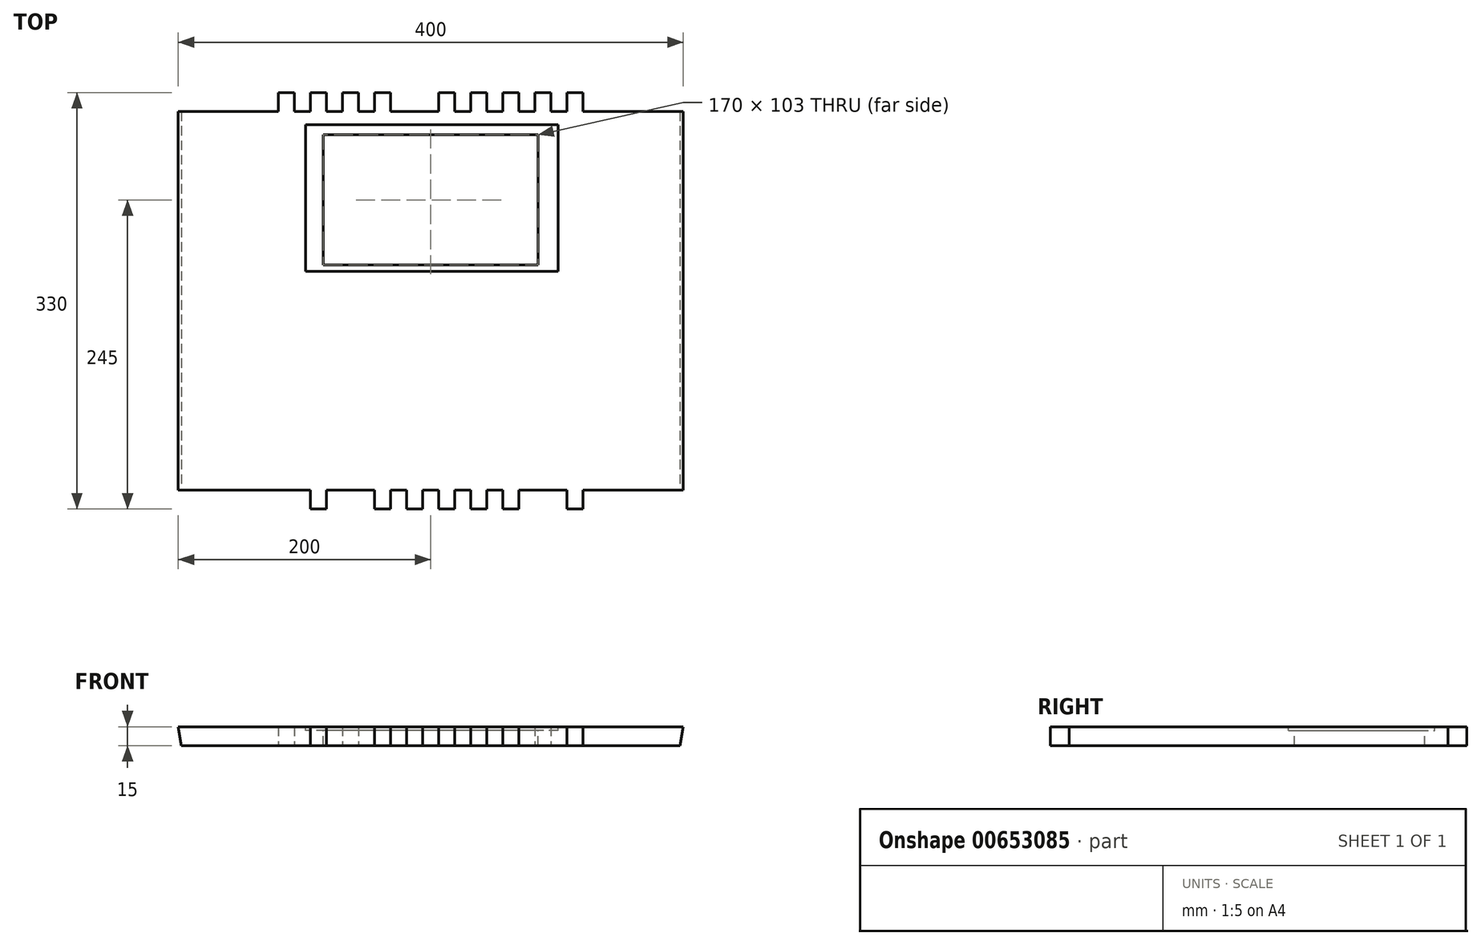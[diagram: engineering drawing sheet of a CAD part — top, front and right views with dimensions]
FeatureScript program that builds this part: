
annotation { "Feature Type Name" : "Feature", "Feature Type Description" : "" }
export const myFeature = defineFeature(function(context is Context, id is Id, definition is map)
    precondition{}
    {
        {
            var Q0;
            Q0=qCreatedBy(makeId("Top.planeOp"),FACE);
            var sketch = newSketch(context, id + "F0", { "sketchPlane" : qUnion([Q0])});
            skLineSegment(sketch, "E0.bottom", {"start": v(200, -150) * mm, "end": v(-200, -150) * mm});
            skLineSegment(sketch, "E0.top", {"start": v(200, 150) * mm, "end": v(-200, 150) * mm});
            skLineSegment(sketch, "E0.left", {"start": v(200, -150) * mm, "end": v(200, 150) * mm});
            skLineSegment(sketch, "E0.right", {"start": v(-200, -150) * mm, "end": v(-200, 150) * mm});
            skPoint(sketch, "E0.middle", {"position": v(0, 0) * mm});
            skLineSegment(sketch, "E1", {"start": v(0, 150) * mm, "end": v(-6.35, 150) * mm});
            skLineSegment(sketch, "E2.bottom", {"start": v(-6.35, 150) * mm, "end": v(-19.05, 150) * mm});
            skLineSegment(sketch, "E2.top", {"start": v(-6.35, 165) * mm, "end": v(-19.05, 165) * mm});
            skLineSegment(sketch, "E2.left", {"start": v(-6.35, 150) * mm, "end": v(-6.35, 165) * mm});
            skLineSegment(sketch, "E2.right", {"start": v(-19.05, 150) * mm, "end": v(-19.05, 165) * mm});
            skLineSegment(sketch, "E3.1.0.0", {"start": v(-31.75, 165) * mm, "end": v(-44.45, 165) * mm});
            skLineSegment(sketch, "E3.1.0.1", {"start": v(-44.45, 150) * mm, "end": v(-44.45, 165) * mm});
            skLineSegment(sketch, "E3.1.0.2", {"start": v(-31.75, 150) * mm, "end": v(-31.75, 165) * mm});
            skLineSegment(sketch, "E3.1.0.3", {"start": v(-31.75, 150) * mm, "end": v(-44.45, 150) * mm});
            skLineSegment(sketch, "E3.2.0.0", {"start": v(-57.15, 165) * mm, "end": v(-69.85, 165) * mm});
            skLineSegment(sketch, "E3.2.0.1", {"start": v(-69.85, 150) * mm, "end": v(-69.85, 165) * mm});
            skLineSegment(sketch, "E3.2.0.2", {"start": v(-57.15, 150) * mm, "end": v(-57.15, 165) * mm});
            skLineSegment(sketch, "E3.2.0.3", {"start": v(-57.15, 150) * mm, "end": v(-69.85, 150) * mm});
            skLineSegment(sketch, "E3.3.0.0", {"start": v(-82.55, 165) * mm, "end": v(-95.25, 165) * mm});
            skLineSegment(sketch, "E3.3.0.1", {"start": v(-95.25, 150) * mm, "end": v(-95.25, 165) * mm});
            skLineSegment(sketch, "E3.3.0.2", {"start": v(-82.55, 150) * mm, "end": v(-82.55, 165) * mm});
            skLineSegment(sketch, "E3.3.0.3", {"start": v(-82.55, 150) * mm, "end": v(-95.25, 150) * mm});
            skLineSegment(sketch, "E3.4.0.0", {"start": v(-107.95, 165) * mm, "end": v(-120.65, 165) * mm});
            skLineSegment(sketch, "E3.4.0.1", {"start": v(-120.65, 150) * mm, "end": v(-120.65, 165) * mm});
            skLineSegment(sketch, "E3.4.0.2", {"start": v(-107.95, 150) * mm, "end": v(-107.95, 165) * mm});
            skLineSegment(sketch, "E3.4.0.3", {"start": v(-107.95, 150) * mm, "end": v(-120.65, 150) * mm});
            skLineSegment(sketch, "E3.direction1", {"start": v(-19.05, 165) * mm, "end": v(-44.45, 165) * mm, "construction": true});
            skLineSegment(sketch, "E4.1.0.0", {"start": v(6.35, 150) * mm, "end": v(6.35, 165) * mm});
            skLineSegment(sketch, "E4.1.0.1", {"start": v(19.05, 165) * mm, "end": v(6.35, 165) * mm});
            skLineSegment(sketch, "E4.1.0.2", {"start": v(19.05, 150) * mm, "end": v(6.35, 150) * mm});
            skLineSegment(sketch, "E4.1.0.3", {"start": v(19.05, 150) * mm, "end": v(19.05, 165) * mm});
            skLineSegment(sketch, "E4.2.0.0", {"start": v(31.75, 150) * mm, "end": v(31.75, 165) * mm});
            skLineSegment(sketch, "E4.2.0.1", {"start": v(44.45, 165) * mm, "end": v(31.75, 165) * mm});
            skLineSegment(sketch, "E4.2.0.2", {"start": v(44.45, 150) * mm, "end": v(31.75, 150) * mm});
            skLineSegment(sketch, "E4.2.0.3", {"start": v(44.45, 150) * mm, "end": v(44.45, 165) * mm});
            skLineSegment(sketch, "E4.3.0.0", {"start": v(57.15, 150) * mm, "end": v(57.15, 165) * mm});
            skLineSegment(sketch, "E4.3.0.1", {"start": v(69.85, 165) * mm, "end": v(57.15, 165) * mm});
            skLineSegment(sketch, "E4.3.0.2", {"start": v(69.85, 150) * mm, "end": v(57.15, 150) * mm});
            skLineSegment(sketch, "E4.3.0.3", {"start": v(69.85, 150) * mm, "end": v(69.85, 165) * mm});
            skLineSegment(sketch, "E4.4.0.0", {"start": v(82.55, 150) * mm, "end": v(82.55, 165) * mm});
            skLineSegment(sketch, "E4.4.0.1", {"start": v(95.25, 165) * mm, "end": v(82.55, 165) * mm});
            skLineSegment(sketch, "E4.4.0.2", {"start": v(95.25, 150) * mm, "end": v(82.55, 150) * mm});
            skLineSegment(sketch, "E4.4.0.3", {"start": v(95.25, 150) * mm, "end": v(95.25, 165) * mm});
            skLineSegment(sketch, "E4.5.0.0", {"start": v(107.95, 150) * mm, "end": v(107.95, 165) * mm});
            skLineSegment(sketch, "E4.5.0.1", {"start": v(120.65, 165) * mm, "end": v(107.95, 165) * mm});
            skLineSegment(sketch, "E4.5.0.2", {"start": v(120.65, 150) * mm, "end": v(107.95, 150) * mm});
            skLineSegment(sketch, "E4.5.0.3", {"start": v(120.65, 150) * mm, "end": v(120.65, 165) * mm});
            skLineSegment(sketch, "E4.direction1", {"start": v(-19.05, 150) * mm, "end": v(6.35, 150) * mm, "construction": true});
            skLineSegment(sketch, "E5.MirrorCS", {"start": v(-19.05, -150) * mm, "end": v(-19.05, -165) * mm});
            skLineSegment(sketch, "E6.MirrorCS", {"start": v(-6.35, -150) * mm, "end": v(-19.05, -150) * mm});
            skLineSegment(sketch, "E7.MirrorCS", {"start": v(-31.75, -165) * mm, "end": v(-44.45, -165) * mm});
            skLineSegment(sketch, "E8.MirrorCS", {"start": v(0, -150) * mm, "end": v(-6.35, -150) * mm});
            skLineSegment(sketch, "E9.MirrorCS", {"start": v(-19.05, -150) * mm, "end": v(6.35, -150) * mm, "construction": true});
            skLineSegment(sketch, "E10.MirrorCS", {"start": v(-44.45, -150) * mm, "end": v(-44.45, -165) * mm});
            skLineSegment(sketch, "E11.MirrorCS", {"start": v(-82.55, -165) * mm, "end": v(-95.25, -165) * mm});
            skLineSegment(sketch, "E12.MirrorCS", {"start": v(44.45, -150) * mm, "end": v(44.45, -165) * mm});
            skLineSegment(sketch, "E13.MirrorCS", {"start": v(44.45, -150) * mm, "end": v(31.75, -150) * mm});
            skLineSegment(sketch, "E14.MirrorCS", {"start": v(-57.15, -150) * mm, "end": v(-69.85, -150) * mm});
            skLineSegment(sketch, "E15.MirrorCS", {"start": v(-82.55, -150) * mm, "end": v(-95.25, -150) * mm});
            skLineSegment(sketch, "E16.MirrorCS", {"start": v(57.15, -150) * mm, "end": v(57.15, -165) * mm});
            skLineSegment(sketch, "E17.MirrorCS", {"start": v(-107.95, -150) * mm, "end": v(-120.65, -150) * mm});
            skLineSegment(sketch, "E18.MirrorCS", {"start": v(95.25, -150) * mm, "end": v(82.55, -150) * mm});
            skLineSegment(sketch, "E19.MirrorCS", {"start": v(-69.85, -150) * mm, "end": v(-69.85, -165) * mm});
            skLineSegment(sketch, "E20.MirrorCS", {"start": v(69.85, -165) * mm, "end": v(57.15, -165) * mm});
            skLineSegment(sketch, "E21.MirrorCS", {"start": v(-82.55, -150) * mm, "end": v(-82.55, -165) * mm});
            skLineSegment(sketch, "E22.MirrorCS", {"start": v(-31.75, -150) * mm, "end": v(-31.75, -165) * mm});
            skLineSegment(sketch, "E23.MirrorCS", {"start": v(-107.95, -150) * mm, "end": v(-107.95, -165) * mm});
            skLineSegment(sketch, "E24.MirrorCS", {"start": v(69.85, -150) * mm, "end": v(57.15, -150) * mm});
            skLineSegment(sketch, "E25.MirrorCS", {"start": v(95.25, -150) * mm, "end": v(95.25, -165) * mm});
            skLineSegment(sketch, "E26.MirrorCS", {"start": v(44.45, -165) * mm, "end": v(31.75, -165) * mm});
            skLineSegment(sketch, "E27.MirrorCS", {"start": v(-120.65, -150) * mm, "end": v(-120.65, -165) * mm});
            skLineSegment(sketch, "E28.MirrorCS", {"start": v(-95.25, -150) * mm, "end": v(-95.25, -165) * mm});
            skLineSegment(sketch, "E29.MirrorCS", {"start": v(120.65, -165) * mm, "end": v(107.95, -165) * mm});
            skLineSegment(sketch, "E30.MirrorCS", {"start": v(19.05, -165) * mm, "end": v(6.35, -165) * mm});
            skLineSegment(sketch, "E31.MirrorCS", {"start": v(-31.75, -150) * mm, "end": v(-44.45, -150) * mm});
            skLineSegment(sketch, "E32.MirrorCS", {"start": v(120.65, -150) * mm, "end": v(120.65, -165) * mm});
            skLineSegment(sketch, "E33.MirrorCS", {"start": v(19.05, -150) * mm, "end": v(19.05, -165) * mm});
            skLineSegment(sketch, "E34.MirrorCS", {"start": v(120.65, -150) * mm, "end": v(107.95, -150) * mm});
            skLineSegment(sketch, "E35.MirrorCS", {"start": v(-107.95, -165) * mm, "end": v(-120.65, -165) * mm});
            skLineSegment(sketch, "E36.MirrorCS", {"start": v(6.35, -150) * mm, "end": v(6.35, -165) * mm});
            skLineSegment(sketch, "E37.MirrorCS", {"start": v(107.95, -150) * mm, "end": v(107.95, -165) * mm});
            skLineSegment(sketch, "E38.MirrorCS", {"start": v(19.05, -150) * mm, "end": v(6.35, -150) * mm});
            skLineSegment(sketch, "E39.MirrorCS", {"start": v(31.75, -150) * mm, "end": v(31.75, -165) * mm});
            skLineSegment(sketch, "E40.MirrorCS", {"start": v(-57.15, -165) * mm, "end": v(-69.85, -165) * mm});
            skLineSegment(sketch, "E41.MirrorCS", {"start": v(-57.15, -150) * mm, "end": v(-57.15, -165) * mm});
            skLineSegment(sketch, "E42.MirrorCS", {"start": v(95.25, -165) * mm, "end": v(82.55, -165) * mm});
            skLineSegment(sketch, "E43.MirrorCS", {"start": v(69.85, -150) * mm, "end": v(69.85, -165) * mm});
            skLineSegment(sketch, "E44.MirrorCS", {"start": v(82.55, -150) * mm, "end": v(82.55, -165) * mm});
            skLineSegment(sketch, "E45.MirrorCS", {"start": v(-19.05, -165) * mm, "end": v(-44.45, -165) * mm, "construction": true});
            skLineSegment(sketch, "E46.MirrorCS", {"start": v(-6.35, -165) * mm, "end": v(-19.05, -165) * mm});
            skLineSegment(sketch, "E47.MirrorCS", {"start": v(-6.35, -150) * mm, "end": v(-6.35, -165) * mm});
            skSolve(sketch);
        }
        {
            var Q0;
            {var subQ15=sQuery(id+"F0.wireOp",EDGE,"E0.left");Q0=makeQuery(id+"F0.imprint","IMPRINT",FACE,{"disambiguationData":[TD([[makeQuery(id+"F0.imprint","IMPRINT",EDGE,{"derivedFrom":subQ15}),1.0]])]});}
            var Q1;
            Q1=makeQuery(id+"F0.imprint","IMPRINT",FACE,{"disambiguationData":[TD([[makeQuery(id+"F0.imprint","IMPRINT",EDGE,{"derivedFrom":sQuery(id+"F0.wireOp",EDGE,"E7.MirrorCS")}),-1.0]])]});
            var Q2;
            Q2=makeQuery(id+"F0.imprint","IMPRINT",FACE,{"disambiguationData":[TD([[makeQuery(id+"F0.imprint","IMPRINT",EDGE,{"derivedFrom":sQuery(id+"F0.wireOp",EDGE,"E4.5.0.0")}),-1.0]])]});
            var Q3;
            Q3=makeQuery(id+"F0.imprint","IMPRINT",FACE,{"disambiguationData":[TD([[makeQuery(id+"F0.imprint","IMPRINT",EDGE,{"derivedFrom":sQuery(id+"F0.wireOp",EDGE,"E17.MirrorCS")}),1.0]])]});
            var Q4;
            Q4=makeQuery(id+"F0.imprint","IMPRINT",FACE,{"disambiguationData":[TD([[makeQuery(id+"F0.imprint","IMPRINT",EDGE,{"derivedFrom":sQuery(id+"F0.wireOp",EDGE,"E29.MirrorCS")}),-1.0]])]});
            var Q5;
            Q5=makeQuery(id+"F0.imprint","IMPRINT",FACE,{"disambiguationData":[TD([[makeQuery(id+"F0.imprint","IMPRINT",EDGE,{"derivedFrom":sQuery(id+"F0.wireOp",EDGE,"E30.MirrorCS")}),-1.0]])]});
            var Q6;
            Q6=makeQuery(id+"F0.imprint","IMPRINT",FACE,{"disambiguationData":[TD([[makeQuery(id+"F0.imprint","IMPRINT",EDGE,{"derivedFrom":sQuery(id+"F0.wireOp",EDGE,"E16.MirrorCS")}),1.0]])]});
            var Q7;
            Q7=makeQuery(id+"F0.imprint","IMPRINT",FACE,{"disambiguationData":[TD([[makeQuery(id+"F0.imprint","IMPRINT",EDGE,{"derivedFrom":sQuery(id+"F0.wireOp",EDGE,"E14.MirrorCS")}),1.0]])]});
            var Q8;
            Q8=makeQuery(id+"F0.imprint","IMPRINT",FACE,{"disambiguationData":[TD([[makeQuery(id+"F0.imprint","IMPRINT",EDGE,{"derivedFrom":sQuery(id+"F0.wireOp",EDGE,"E3.2.0.0")}),1.0]])]});
            var Q9;
            Q9=makeQuery(id+"F0.imprint","IMPRINT",FACE,{"disambiguationData":[TD([[makeQuery(id+"F0.imprint","IMPRINT",EDGE,{"derivedFrom":sQuery(id+"F0.wireOp",EDGE,"E4.1.0.0")}),-1.0]])]});
            var Q10;
            Q10=makeQuery(id+"F0.imprint","IMPRINT",FACE,{"disambiguationData":[TD([[makeQuery(id+"F0.imprint","IMPRINT",EDGE,{"derivedFrom":sQuery(id+"F0.wireOp",EDGE,"E3.3.0.0")}),1.0]])]});
            var Q11;
            Q11=makeQuery(id+"F0.imprint","IMPRINT",FACE,{"disambiguationData":[TD([[makeQuery(id+"F0.imprint","IMPRINT",EDGE,{"derivedFrom":sQuery(id+"F0.wireOp",EDGE,"E11.MirrorCS")}),-1.0]])]});
            var Q12;
            Q12=makeQuery(id+"F0.imprint","IMPRINT",FACE,{"disambiguationData":[TD([[makeQuery(id+"F0.imprint","IMPRINT",EDGE,{"derivedFrom":sQuery(id+"F0.wireOp",EDGE,"E4.2.0.0")}),-1.0]])]});
            var Q13;
            Q13=makeQuery(id+"F0.imprint","IMPRINT",FACE,{"disambiguationData":[TD([[makeQuery(id+"F0.imprint","IMPRINT",EDGE,{"derivedFrom":sQuery(id+"F0.wireOp",EDGE,"E18.MirrorCS")}),1.0]])]});
            var Q14;
            Q14=makeQuery(id+"F0.imprint","IMPRINT",FACE,{"disambiguationData":[TD([[makeQuery(id+"F0.imprint","IMPRINT",EDGE,{"derivedFrom":sQuery(id+"F0.wireOp",EDGE,"E12.MirrorCS")}),-1.0]])]});
            var Q15;
            Q15=makeQuery(id+"F0.imprint","IMPRINT",FACE,{"disambiguationData":[TD([[makeQuery(id+"F0.imprint","IMPRINT",EDGE,{"derivedFrom":sQuery(id+"F0.wireOp",EDGE,"E3.1.0.0")}),1.0]])]});
            var Q16;
            Q16=makeQuery(id+"F0.imprint","IMPRINT",FACE,{"disambiguationData":[TD([[makeQuery(id+"F0.imprint","IMPRINT",EDGE,{"derivedFrom":sQuery(id+"F0.wireOp",EDGE,"E3.4.0.0")}),1.0]])]});
            var Q17;
            Q17=makeQuery(id+"F0.imprint","IMPRINT",FACE,{"disambiguationData":[TD([[makeQuery(id+"F0.imprint","IMPRINT",EDGE,{"derivedFrom":sQuery(id+"F0.wireOp",EDGE,"E4.4.0.0")}),-1.0]])]});
            var Q18;
            Q18=makeQuery(id+"F0.imprint","IMPRINT",FACE,{"disambiguationData":[TD([[makeQuery(id+"F0.imprint","IMPRINT",EDGE,{"derivedFrom":sQuery(id+"F0.wireOp",EDGE,"E4.3.0.0")}),-1.0]])]});
            var Q19;
            Q19=makeQuery(id+"F0.imprint","IMPRINT",FACE,{"disambiguationData":[TD([[makeQuery(id+"F0.imprint","IMPRINT",EDGE,{"derivedFrom":sQuery(id+"F0.wireOp",EDGE,"E2.bottom")}),-1.0]])]});
            var Q20;
            Q20=makeQuery(id+"F0.imprint","IMPRINT",FACE,{"disambiguationData":[TD([[makeQuery(id+"F0.imprint","IMPRINT",EDGE,{"derivedFrom":sQuery(id+"F0.wireOp",EDGE,"E5.MirrorCS")}),1.0]])]});
            extrude(context, id + "F1", {"entities" : qUnion([Q0, Q1, Q2, Q3, Q4, Q5, Q6, Q7, Q8, Q9, Q10, Q11, Q12, Q13, Q14, Q15, Q16, Q17, Q18, Q19, Q20]), "depth" : 15 * mm, "offsetDistance" : 25 * mm});
        }
        {
            var Q0;
            {var subQ0=sQuery(id+"F0.wireOp",EDGE,"E0.bottom");Q0=makeQuery(id+"F1.opExtrude","SWEPT_FACE",FACE,{"disambiguationData":[OSD([subQ0]),TDD([makeQuery(id+"F0.imprint","IMPRINT",EDGE,{"disambiguationData":[TD([[makeQuery(id+"F0.imprint","INTERSECT",VERTEX,{"derivedFrom":[subQ0,sQuery(id+"F0.wireOp",EDGE,"E0.right")]}),1.0]])],"derivedFrom":subQ0})])]});}
            var sketch = newSketch(context, id + "F2", { "sketchPlane" : qUnion([Q0])});
            skLineSegment(sketch, "E48", {"start": v(-197.5, 0) * mm, "end": v(-200, 0) * mm});
            skLineSegment(sketch, "E49", {"start": v(-200, 0) * mm, "end": v(-200, 15) * mm});
            skLineSegment(sketch, "E50", {"start": v(-200, 15) * mm, "end": v(-197.5, 0) * mm});
            skSolve(sketch);
        }
        {
            var Q0;
            Q0=makeQuery(id+"F2.imprint","IMPRINT",FACE,{"disambiguationData":[TD([[makeQuery(id+"F2.imprint","IMPRINT",EDGE,{"derivedFrom":sQuery(id+"F2.wireOp",EDGE,"E48")}),-1.0]])]});
            extrude(context, id + "F3", {"entities" : qUnion([Q0]), "operationType" : NewBodyOperationType.REMOVE, "endBound" : BoundingType.THROUGH_ALL, "oppositeDirection" : true, "depth" : 25 * mm, "offsetDistance" : 25 * mm});
        }
        {
            var Q0;
            {var subQ0=sQuery(id+"F0.wireOp",EDGE,"E0.bottom");Q0=makeQuery(id+"F1.opExtrude","SWEPT_FACE",FACE,{"disambiguationData":[OSD([subQ0]),TDD([makeQuery(id+"F0.imprint","IMPRINT",EDGE,{"disambiguationData":[TD([[makeQuery(id+"F0.imprint","INTERSECT",VERTEX,{"derivedFrom":[subQ0,sQuery(id+"F0.wireOp",EDGE,"E0.left")]}),-1.0]])],"derivedFrom":subQ0})])]});}
            var sketch = newSketch(context, id + "F4", { "sketchPlane" : qUnion([Q0])});
            skLineSegment(sketch, "E51", {"start": v(197.5, 0) * mm, "end": v(200, 0) * mm});
            skLineSegment(sketch, "E52", {"start": v(200, 0) * mm, "end": v(200, 15) * mm});
            skLineSegment(sketch, "E53", {"start": v(200, 15) * mm, "end": v(197.5, 0) * mm});
            skSolve(sketch);
        }
        {
            var Q0;
            Q0=makeQuery(id+"F4.imprint","IMPRINT",FACE,{"disambiguationData":[TD([[makeQuery(id+"F4.imprint","IMPRINT",EDGE,{"derivedFrom":sQuery(id+"F4.wireOp",EDGE,"E51")}),-1.0]])]});
            extrude(context, id + "F5", {"entities" : qUnion([Q0]), "operationType" : NewBodyOperationType.REMOVE, "endBound" : BoundingType.THROUGH_ALL, "oppositeDirection" : true, "depth" : 25 * mm, "offsetDistance" : 25 * mm});
        }
        {
            var Q0;
            Q0=makeQuery(id+"F1.opExtrude","CAP_FACE",FACE,{"disambiguationData":[OSD([sQuery(id+"F0.wireOp",EDGE,"E0.bottom"),sQuery(id+"F0.wireOp",EDGE,"E0.top"),sQuery(id+"F0.wireOp",EDGE,"E0.left"),sQuery(id+"F0.wireOp",EDGE,"E0.right"),sQuery(id+"F0.wireOp",EDGE,"E1"),sQuery(id+"F0.wireOp",EDGE,"E2.top"),sQuery(id+"F0.wireOp",EDGE,"E2.left"),sQuery(id+"F0.wireOp",EDGE,"E2.right"),sQuery(id+"F0.wireOp",EDGE,"E3.1.0.0"),sQuery(id+"F0.wireOp",EDGE,"E3.1.0.1"),sQuery(id+"F0.wireOp",EDGE,"E3.1.0.2"),sQuery(id+"F0.wireOp",EDGE,"E3.2.0.0"),sQuery(id+"F0.wireOp",EDGE,"E3.2.0.1"),sQuery(id+"F0.wireOp",EDGE,"E3.2.0.2"),sQuery(id+"F0.wireOp",EDGE,"E3.3.0.0"),sQuery(id+"F0.wireOp",EDGE,"E3.3.0.1"),sQuery(id+"F0.wireOp",EDGE,"E3.3.0.2"),sQuery(id+"F0.wireOp",EDGE,"E3.4.0.0"),sQuery(id+"F0.wireOp",EDGE,"E3.4.0.1"),sQuery(id+"F0.wireOp",EDGE,"E3.4.0.2"),sQuery(id+"F0.wireOp",EDGE,"E4.1.0.0"),sQuery(id+"F0.wireOp",EDGE,"E4.1.0.1"),sQuery(id+"F0.wireOp",EDGE,"E4.1.0.3"),sQuery(id+"F0.wireOp",EDGE,"E4.2.0.0"),sQuery(id+"F0.wireOp",EDGE,"E4.2.0.1"),sQuery(id+"F0.wireOp",EDGE,"E4.2.0.3"),sQuery(id+"F0.wireOp",EDGE,"E4.3.0.0"),sQuery(id+"F0.wireOp",EDGE,"E4.3.0.1"),sQuery(id+"F0.wireOp",EDGE,"E4.3.0.3"),sQuery(id+"F0.wireOp",EDGE,"E4.4.0.0"),sQuery(id+"F0.wireOp",EDGE,"E4.4.0.1"),sQuery(id+"F0.wireOp",EDGE,"E4.4.0.3"),sQuery(id+"F0.wireOp",EDGE,"E4.5.0.0"),sQuery(id+"F0.wireOp",EDGE,"E4.5.0.1"),sQuery(id+"F0.wireOp",EDGE,"E4.5.0.3"),sQuery(id+"F0.wireOp",EDGE,"E5.MirrorCS"),sQuery(id+"F0.wireOp",EDGE,"E7.MirrorCS"),sQuery(id+"F0.wireOp",EDGE,"E8.MirrorCS"),sQuery(id+"F0.wireOp",EDGE,"E10.MirrorCS"),sQuery(id+"F0.wireOp",EDGE,"E11.MirrorCS"),sQuery(id+"F0.wireOp",EDGE,"E12.MirrorCS"),sQuery(id+"F0.wireOp",EDGE,"E16.MirrorCS"),sQuery(id+"F0.wireOp",EDGE,"E19.MirrorCS"),sQuery(id+"F0.wireOp",EDGE,"E20.MirrorCS"),sQuery(id+"F0.wireOp",EDGE,"E21.MirrorCS"),sQuery(id+"F0.wireOp",EDGE,"E22.MirrorCS"),sQuery(id+"F0.wireOp",EDGE,"E23.MirrorCS"),sQuery(id+"F0.wireOp",EDGE,"E25.MirrorCS"),sQuery(id+"F0.wireOp",EDGE,"E26.MirrorCS"),sQuery(id+"F0.wireOp",EDGE,"E27.MirrorCS"),sQuery(id+"F0.wireOp",EDGE,"E28.MirrorCS"),sQuery(id+"F0.wireOp",EDGE,"E29.MirrorCS"),sQuery(id+"F0.wireOp",EDGE,"E30.MirrorCS"),sQuery(id+"F0.wireOp",EDGE,"E32.MirrorCS"),sQuery(id+"F0.wireOp",EDGE,"E33.MirrorCS"),sQuery(id+"F0.wireOp",EDGE,"E35.MirrorCS"),sQuery(id+"F0.wireOp",EDGE,"E36.MirrorCS"),sQuery(id+"F0.wireOp",EDGE,"E37.MirrorCS"),sQuery(id+"F0.wireOp",EDGE,"E39.MirrorCS"),sQuery(id+"F0.wireOp",EDGE,"E40.MirrorCS"),sQuery(id+"F0.wireOp",EDGE,"E41.MirrorCS"),sQuery(id+"F0.wireOp",EDGE,"E42.MirrorCS"),sQuery(id+"F0.wireOp",EDGE,"E43.MirrorCS"),sQuery(id+"F0.wireOp",EDGE,"E44.MirrorCS"),sQuery(id+"F0.wireOp",EDGE,"E46.MirrorCS"),sQuery(id+"F0.wireOp",EDGE,"E47.MirrorCS")])],"isStart":false});
            var sketch = newSketch(context, id + "F6", { "sketchPlane" : qUnion([Q0])});
            skLineSegment(sketch, "E54.bottom", {"start": v(85, 28.5) * mm, "end": v(-85, 28.5) * mm});
            skLineSegment(sketch, "E54.top", {"start": v(85, 131.5) * mm, "end": v(-85, 131.5) * mm});
            skLineSegment(sketch, "E54.left", {"start": v(85, 28.5) * mm, "end": v(85, 131.5) * mm});
            skLineSegment(sketch, "E54.right", {"start": v(-85, 28.5) * mm, "end": v(-85, 131.5) * mm});
            skPoint(sketch, "E54.middle", {"position": v(0, 80) * mm});
            skSolve(sketch);
        }
        {
            var Q0;
            Q0=makeQuery(id+"F6.imprint","IMPRINT",FACE,{"disambiguationData":[TD([[makeQuery(id+"F6.imprint","IMPRINT",EDGE,{"derivedFrom":sQuery(id+"F6.wireOp",EDGE,"E54.bottom")}),-1.0]])]});
            extrude(context, id + "F7", {"entities" : qUnion([Q0]), "operationType" : NewBodyOperationType.REMOVE, "oppositeDirection" : true, "depth" : 15 * mm, "offsetDistance" : 25 * mm});
        }
        {
            var Q0;
            Q0=makeQuery(id+"F1.opExtrude","CAP_FACE",FACE,{"disambiguationData":[OSD([sQuery(id+"F0.wireOp",EDGE,"E0.bottom"),sQuery(id+"F0.wireOp",EDGE,"E0.top"),sQuery(id+"F0.wireOp",EDGE,"E0.left"),sQuery(id+"F0.wireOp",EDGE,"E0.right"),sQuery(id+"F0.wireOp",EDGE,"E1"),sQuery(id+"F0.wireOp",EDGE,"E2.top"),sQuery(id+"F0.wireOp",EDGE,"E2.left"),sQuery(id+"F0.wireOp",EDGE,"E2.right"),sQuery(id+"F0.wireOp",EDGE,"E3.1.0.0"),sQuery(id+"F0.wireOp",EDGE,"E3.1.0.1"),sQuery(id+"F0.wireOp",EDGE,"E3.1.0.2"),sQuery(id+"F0.wireOp",EDGE,"E3.2.0.0"),sQuery(id+"F0.wireOp",EDGE,"E3.2.0.1"),sQuery(id+"F0.wireOp",EDGE,"E3.2.0.2"),sQuery(id+"F0.wireOp",EDGE,"E3.3.0.0"),sQuery(id+"F0.wireOp",EDGE,"E3.3.0.1"),sQuery(id+"F0.wireOp",EDGE,"E3.3.0.2"),sQuery(id+"F0.wireOp",EDGE,"E3.4.0.0"),sQuery(id+"F0.wireOp",EDGE,"E3.4.0.1"),sQuery(id+"F0.wireOp",EDGE,"E3.4.0.2"),sQuery(id+"F0.wireOp",EDGE,"E4.1.0.0"),sQuery(id+"F0.wireOp",EDGE,"E4.1.0.1"),sQuery(id+"F0.wireOp",EDGE,"E4.1.0.3"),sQuery(id+"F0.wireOp",EDGE,"E4.2.0.0"),sQuery(id+"F0.wireOp",EDGE,"E4.2.0.1"),sQuery(id+"F0.wireOp",EDGE,"E4.2.0.3"),sQuery(id+"F0.wireOp",EDGE,"E4.3.0.0"),sQuery(id+"F0.wireOp",EDGE,"E4.3.0.1"),sQuery(id+"F0.wireOp",EDGE,"E4.3.0.3"),sQuery(id+"F0.wireOp",EDGE,"E4.4.0.0"),sQuery(id+"F0.wireOp",EDGE,"E4.4.0.1"),sQuery(id+"F0.wireOp",EDGE,"E4.4.0.3"),sQuery(id+"F0.wireOp",EDGE,"E4.5.0.0"),sQuery(id+"F0.wireOp",EDGE,"E4.5.0.1"),sQuery(id+"F0.wireOp",EDGE,"E4.5.0.3"),sQuery(id+"F0.wireOp",EDGE,"E5.MirrorCS"),sQuery(id+"F0.wireOp",EDGE,"E7.MirrorCS"),sQuery(id+"F0.wireOp",EDGE,"E8.MirrorCS"),sQuery(id+"F0.wireOp",EDGE,"E10.MirrorCS"),sQuery(id+"F0.wireOp",EDGE,"E11.MirrorCS"),sQuery(id+"F0.wireOp",EDGE,"E12.MirrorCS"),sQuery(id+"F0.wireOp",EDGE,"E16.MirrorCS"),sQuery(id+"F0.wireOp",EDGE,"E19.MirrorCS"),sQuery(id+"F0.wireOp",EDGE,"E20.MirrorCS"),sQuery(id+"F0.wireOp",EDGE,"E21.MirrorCS"),sQuery(id+"F0.wireOp",EDGE,"E22.MirrorCS"),sQuery(id+"F0.wireOp",EDGE,"E23.MirrorCS"),sQuery(id+"F0.wireOp",EDGE,"E25.MirrorCS"),sQuery(id+"F0.wireOp",EDGE,"E26.MirrorCS"),sQuery(id+"F0.wireOp",EDGE,"E27.MirrorCS"),sQuery(id+"F0.wireOp",EDGE,"E28.MirrorCS"),sQuery(id+"F0.wireOp",EDGE,"E29.MirrorCS"),sQuery(id+"F0.wireOp",EDGE,"E30.MirrorCS"),sQuery(id+"F0.wireOp",EDGE,"E32.MirrorCS"),sQuery(id+"F0.wireOp",EDGE,"E33.MirrorCS"),sQuery(id+"F0.wireOp",EDGE,"E35.MirrorCS"),sQuery(id+"F0.wireOp",EDGE,"E36.MirrorCS"),sQuery(id+"F0.wireOp",EDGE,"E37.MirrorCS"),sQuery(id+"F0.wireOp",EDGE,"E39.MirrorCS"),sQuery(id+"F0.wireOp",EDGE,"E40.MirrorCS"),sQuery(id+"F0.wireOp",EDGE,"E41.MirrorCS"),sQuery(id+"F0.wireOp",EDGE,"E42.MirrorCS"),sQuery(id+"F0.wireOp",EDGE,"E43.MirrorCS"),sQuery(id+"F0.wireOp",EDGE,"E44.MirrorCS"),sQuery(id+"F0.wireOp",EDGE,"E46.MirrorCS"),sQuery(id+"F0.wireOp",EDGE,"E47.MirrorCS")])],"isStart":false});
            var sketch = newSketch(context, id + "F8", { "sketchPlane" : qUnion([Q0])});
            skLineSegment(sketch, "E55.bottom", {"start": v(101, 23.5) * mm, "end": v(-99, 23.5) * mm});
            skLineSegment(sketch, "E55.top", {"start": v(101, 139.5) * mm, "end": v(-99, 139.5) * mm});
            skLineSegment(sketch, "E55.left", {"start": v(101, 23.5) * mm, "end": v(101, 139.5) * mm});
            skLineSegment(sketch, "E55.right", {"start": v(-99, 23.5) * mm, "end": v(-99, 139.5) * mm});
            skSolve(sketch);
        }
        {
            var Q0;
            Q0=makeQuery(id+"F8.imprint","IMPRINT",FACE,{"disambiguationData":[TD([[makeQuery(id+"F8.imprint","IMPRINT",EDGE,{"derivedFrom":sQuery(id+"F8.wireOp",EDGE,"E55.bottom")}),-1.0]])]});
            extrude(context, id + "F9", {"entities" : qUnion([Q0]), "operationType" : NewBodyOperationType.REMOVE, "oppositeDirection" : true, "depth" : 3 * mm, "offsetDistance" : 25 * mm});
        }
    });
